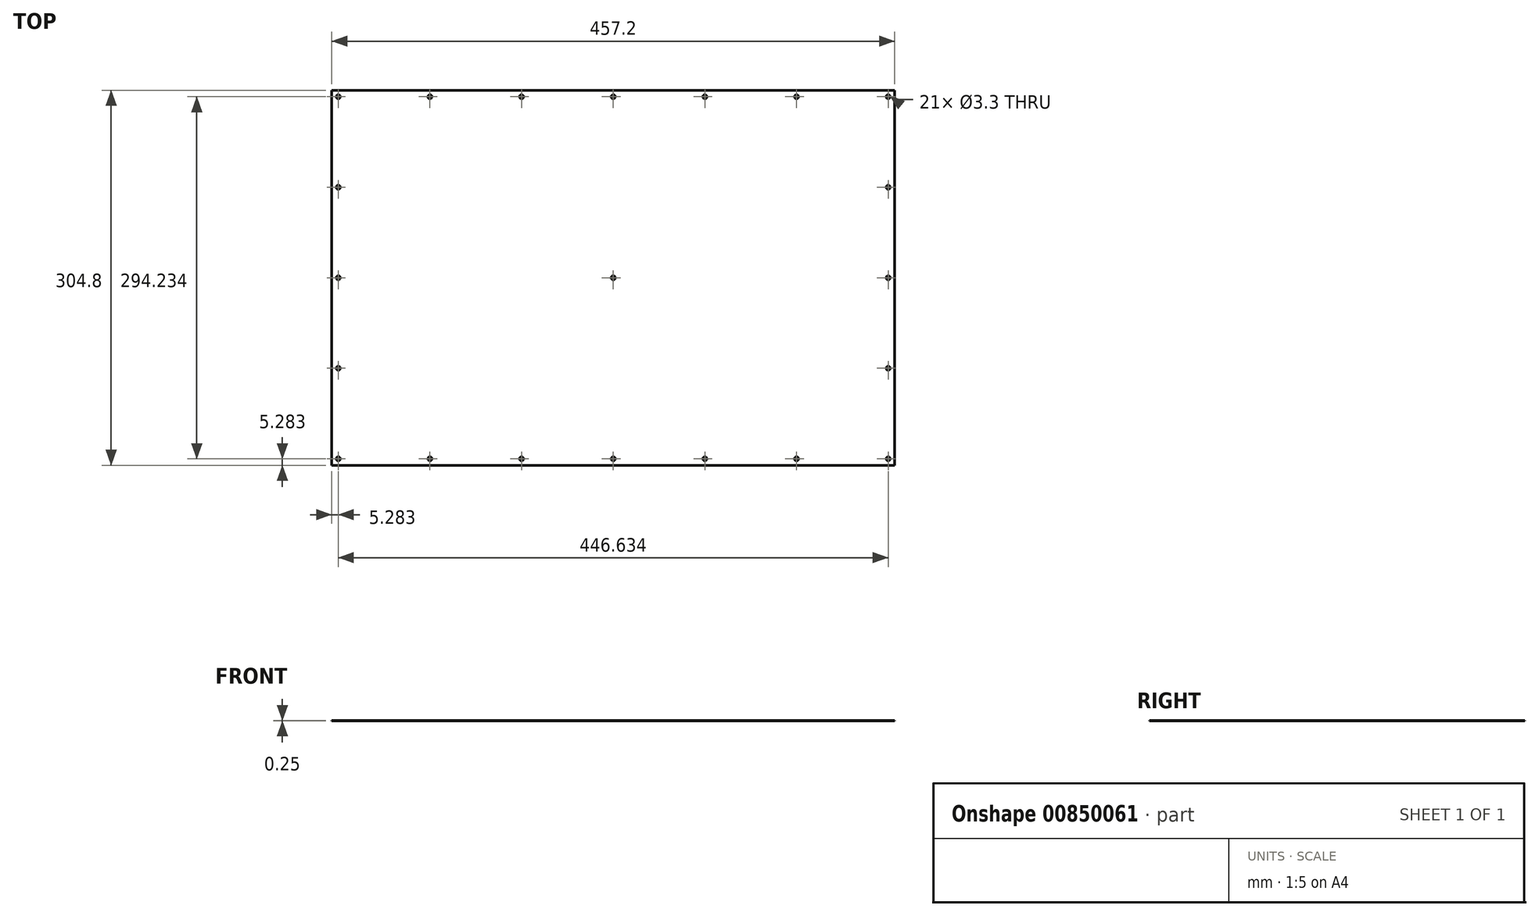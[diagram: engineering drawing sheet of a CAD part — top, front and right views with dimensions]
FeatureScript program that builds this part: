
annotation { "Feature Type Name" : "Feature", "Feature Type Description" : "" }
export const myFeature = defineFeature(function(context is Context, id is Id, definition is map)
    precondition{}
    {
        {
            assignVariable(context, id + "F0", {"name" : "top_Thickness", "anyValue" : .25});
        }
        {
            var Q0;
            Q0=qCreatedBy(makeId("Top.planeOp"),FACE);
            var sketch = newSketch(context, id + "F1", { "sketchPlane" : qUnion([Q0])});
            skLineSegment(sketch, "E0.bottom", {"start": v(228.6, -152.4) * mm, "end": v(-228.6, -152.4) * mm});
            skLineSegment(sketch, "E0.top", {"start": v(228.6, 152.4) * mm, "end": v(-228.6, 152.4) * mm});
            skLineSegment(sketch, "E0.left", {"start": v(228.6, -152.4) * mm, "end": v(228.6, 152.4) * mm});
            skLineSegment(sketch, "E0.right", {"start": v(-228.6, -152.4) * mm, "end": v(-228.6, 152.4) * mm});
            skPoint(sketch, "E0.middle", {"position": v(0, 0) * mm});
            skSolve(sketch);
        }
        {
            var Q0;
            Q0 = qSketchRegion(id + "F1", true);
            extrude(context, id + "F2", {"entities" : qUnion([Q0]), "depth" : (getVariable(context, 'top_Thickness')) * mm, "offsetDistance" : 25.4 * mm});
        }
        {
            var Q0;
            Q0=makeQuery(id+"F2.opExtrude","CAP_FACE",FACE,{"disambiguationData":[OSD([sQuery(id+"F1.wireOp",EDGE,"E0.bottom"),sQuery(id+"F1.wireOp",EDGE,"E0.top"),sQuery(id+"F1.wireOp",EDGE,"E0.left"),sQuery(id+"F1.wireOp",EDGE,"E0.right")])],"isStart":false});
            var sketch = newSketch(context, id + "F3", { "sketchPlane" : qUnion([Q0])});
            skPoint(sketch, "E1", {"position": v(-223.32, 147.12) * mm});
            skPoint(sketch, "E2", {"position": v(-223.32, 73.56) * mm});
            skPoint(sketch, "E3", {"position": v(-223.32, 0) * mm});
            skPoint(sketch, "E4", {"position": v(-223.32, -73.56) * mm});
            skPoint(sketch, "E5", {"position": v(-223.32, -147.12) * mm});
            skLineSegment(sketch, "E6", {"start": v(0, 195.79) * mm, "end": v(0, -204.4) * mm, "construction": true});
            skPoint(sketch, "E7", {"position": v(-148.88, 147.12) * mm});
            skPoint(sketch, "E8", {"position": v(-74.44, 147.12) * mm});
            skPoint(sketch, "E9", {"position": v(0, 147.12) * mm});
            skLineSegment(sketch, "E10", {"start": v(-342.96, 0) * mm, "end": v(336.85, 0) * mm});
            skPoint(sketch, "E11.MirrorP", {"position": v(-148.88, -147.12) * mm});
            skPoint(sketch, "E12.MirrorP", {"position": v(-74.44, -147.12) * mm});
            skPoint(sketch, "E13.MirrorP", {"position": v(0, -147.12) * mm});
            skPoint(sketch, "E14.MirrorP", {"position": v(74.44, 147.12) * mm});
            skPoint(sketch, "E15.MirrorP", {"position": v(74.44, -147.12) * mm});
            skPoint(sketch, "E16.MirrorP", {"position": v(148.88, -147.12) * mm});
            skPoint(sketch, "E17.MirrorP", {"position": v(223.32, -147.12) * mm});
            skPoint(sketch, "E18.MirrorP", {"position": v(223.32, -73.56) * mm});
            skPoint(sketch, "E19.MirrorP", {"position": v(223.32, 0) * mm});
            skPoint(sketch, "E20.MirrorP", {"position": v(223.32, 73.56) * mm});
            skPoint(sketch, "E21.MirrorP", {"position": v(223.32, 147.12) * mm});
            skPoint(sketch, "E22.MirrorP", {"position": v(148.88, 147.12) * mm});
            skPoint(sketch, "E23", {"position": v(0, 0) * mm});
            skSolve(sketch);
        }
        {
            var Q0;
            Q0=sQuery(id+"F3.wireOp",VERTEX,"E1");
            var Q1;
            Q1=sQuery(id+"F3.wireOp",VERTEX,"E7");
            var Q2;
            Q2=sQuery(id+"F3.wireOp",VERTEX,"E8");
            var Q3;
            Q3=sQuery(id+"F3.wireOp",VERTEX,"E9");
            var Q4;
            Q4=sQuery(id+"F3.wireOp",VERTEX,"E14.MirrorP");
            var Q5;
            Q5=sQuery(id+"F3.wireOp",VERTEX,"E22.MirrorP");
            var Q6;
            Q6=sQuery(id+"F3.wireOp",VERTEX,"E21.MirrorP");
            var Q7;
            Q7=sQuery(id+"F3.wireOp",VERTEX,"E20.MirrorP");
            var Q8;
            Q8=sQuery(id+"F3.wireOp",VERTEX,"E19.MirrorP");
            var Q9;
            Q9=sQuery(id+"F3.wireOp",VERTEX,"E18.MirrorP");
            var Q10;
            Q10=sQuery(id+"F3.wireOp",VERTEX,"E17.MirrorP");
            var Q11;
            Q11=sQuery(id+"F3.wireOp",VERTEX,"E16.MirrorP");
            var Q12;
            Q12=sQuery(id+"F3.wireOp",VERTEX,"E15.MirrorP");
            var Q13;
            Q13=sQuery(id+"F3.wireOp",VERTEX,"E13.MirrorP");
            var Q14;
            Q14=sQuery(id+"F3.wireOp",VERTEX,"E12.MirrorP");
            var Q15;
            Q15=sQuery(id+"F3.wireOp",VERTEX,"E11.MirrorP");
            var Q16;
            Q16=sQuery(id+"F3.wireOp",VERTEX,"E4");
            var Q17;
            Q17=sQuery(id+"F3.wireOp",VERTEX,"E5");
            var Q18;
            Q18=sQuery(id+"F3.wireOp",VERTEX,"E3");
            var Q19;
            Q19=sQuery(id+"F3.wireOp",VERTEX,"E2");
            var Q20;
            Q20=sQuery(id+"F3.wireOp",VERTEX,"E23");
            var Q21;
            Q21=makeQuery(id+"F2.opExtrude","SWEPT_BODY",BODY,{"disambiguationData":[OSD([sQuery(id+"F1.wireOp",EDGE,"E0.bottom"),sQuery(id+"F1.wireOp",EDGE,"E0.top"),sQuery(id+"F1.wireOp",EDGE,"E0.left"),sQuery(id+"F1.wireOp",EDGE,"E0.right")])]});
            hole(context, id + "F4", {"style" : HoleStyle.SIMPLE, "endStyle" : HoleEndStyle.THROUGH, "standardTappedOrClearance" : lookupTablePath({ "standard" : "ISO", "engagement" : "75%", "pitch" : "0.7 mm", "size" : "M4", "type" : "Tapped" }), "standardBlindInLast" : lookupTablePath({ "standard" : "ISO", "engagement" : "75%", "pitch" : "0.7 mm", "size" : "M4", "type" : "Tapped" }), "holeDiameter" : 3.3 * mm, "majorDiameter" : 4 * mm, "showTappedDepth" : true, "isTappedThrough" : true, "tappedDepth" : 6.35 * mm, "tapClearance" : 3, "locations" : qUnion([Q0, Q1, Q2, Q3, Q4, Q5, Q6, Q7, Q8, Q9, Q10, Q11, Q12, Q13, Q14, Q15, Q16, Q17, Q18, Q19, Q20]), "scope" : qUnion([Q21])});
        }
    });
